# Revit family: B-683
name_source: partatom
category: Plumbing Fixtures
revit_build: Autodesk Revit 2014 (Build: 20130308_1515(x64)
units: mm (PartAtom-declared; Revit-internal decimal feet)

## types (1)
- B-683
    ADA Compliant = Yes
    CW Connection = No
    CWFU = 0
    Default Elevation = 40"
    Description = Surface-mounted shelf shall be type-304 stainless steel with bright polished finish. Flanges and support arms
    HW Connection = No
    HWFU = 0
    Height = 0"
    Installation Type = Surface Mounted
    Length = 26"
    Manufacturer = Bobrick
    Material = Stainless Steel, Satin finish
    Model = B-683
    Price = Prices may vary. Please consult Manufacturer Representative for most up-to-date price list.
    Product Documentation Link = http://bobrick.com
    Product Page URL = http://bobrick.com
    URL = http://bobrick.com
    Vent Connection = No
    WFU = 0
    Warranty Information = 3 Year Warranty
    Waste Connection = No
    Width = 5 3/4"

## geometry (parser evidence)
native form markers: Sweep x3
no freeform markers — native parametric forms only
